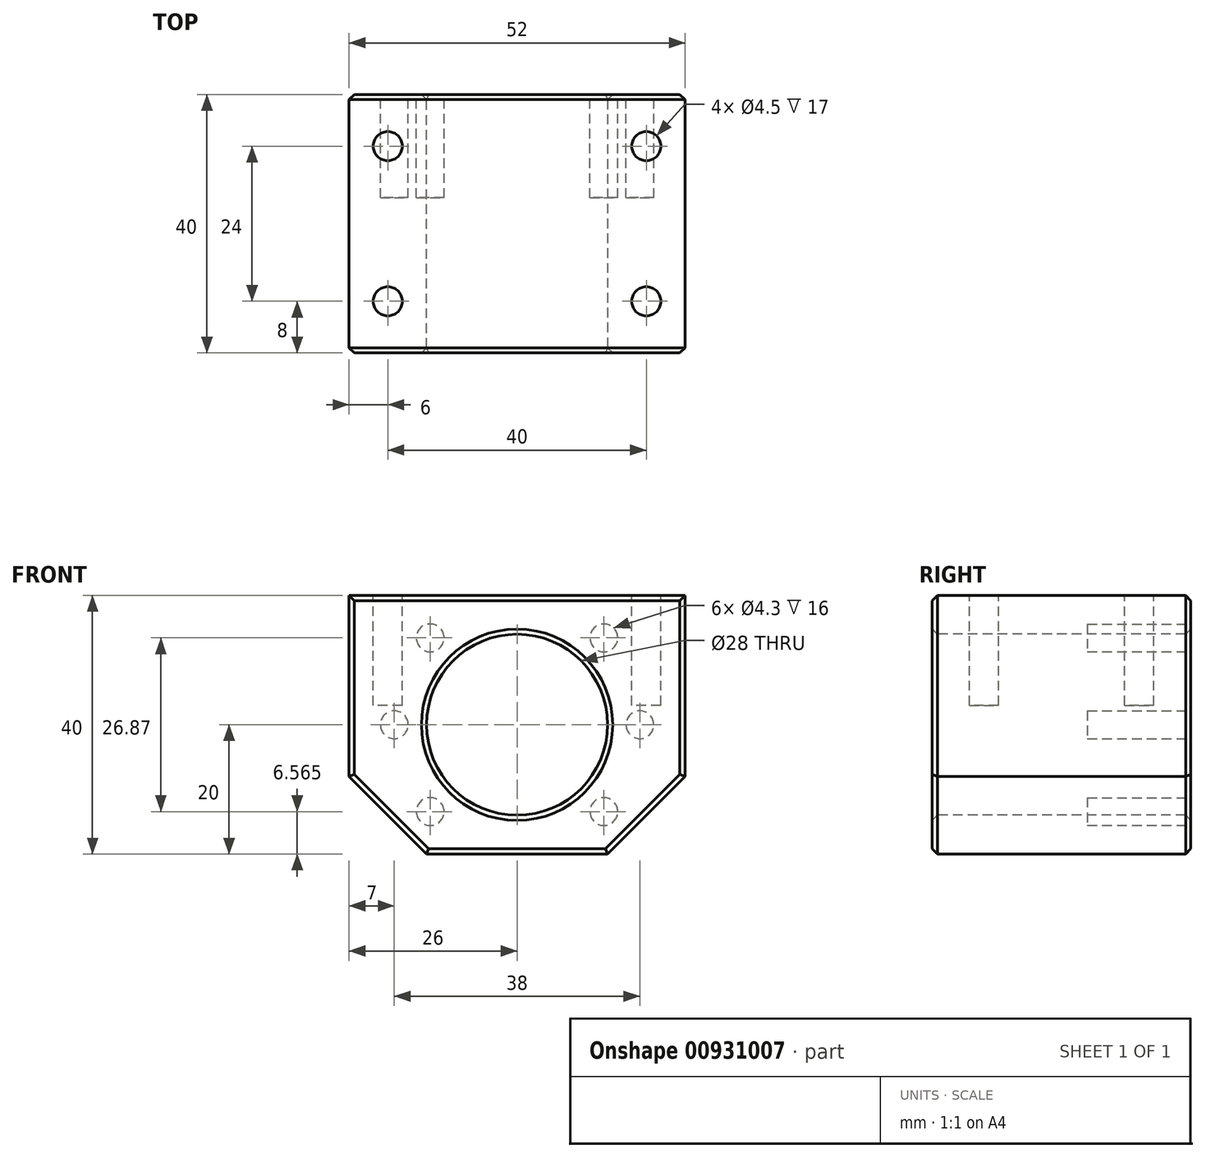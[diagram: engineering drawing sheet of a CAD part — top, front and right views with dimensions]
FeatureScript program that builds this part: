
annotation { "Feature Type Name" : "Feature", "Feature Type Description" : "" }
export const myFeature = defineFeature(function(context is Context, id is Id, definition is map)
    precondition{}
    {
        {
            var Q0;
            Q0=qCreatedBy(makeId("Top.planeOp"),FACE);
            var sketch = newSketch(context, id + "F0", { "sketchPlane" : qUnion([Q0])});
            skLineSegment(sketch, "E0.bottom", {"start": v(-26, -20) * mm, "end": v(26, -20) * mm});
            skLineSegment(sketch, "E0.top", {"start": v(-26, 20) * mm, "end": v(26, 20) * mm});
            skLineSegment(sketch, "E0.left", {"start": v(-26, -20) * mm, "end": v(-26, 20) * mm});
            skLineSegment(sketch, "E0.right", {"start": v(26, -20) * mm, "end": v(26, 20) * mm});
            skPoint(sketch, "E0.middle", {"position": v(0, 0) * mm});
            skSolve(sketch);
        }
        {
            var Q0;
            Q0=makeQuery(id+"F0.imprint","IMPRINT",FACE,{"disambiguationData":[TD([[makeQuery(id+"F0.imprint","IMPRINT",EDGE,{"derivedFrom":sQuery(id+"F0.wireOp",EDGE,"E0.bottom")}),1.0]])]});
            extrude(context, id + "F1", {"entities" : qUnion([Q0]), "depth" : 40 * mm, "offsetDistance" : 25 * mm});
        }
        {
            var Q0;
            Q0=makeQuery(id+"F1.opExtrude","SWEPT_FACE",FACE,{"disambiguationData":[OSD([sQuery(id+"F0.wireOp",EDGE,"E0.bottom")])]});
            var sketch = newSketch(context, id + "F2", { "sketchPlane" : qUnion([Q0])});
            skCircle(sketch, "E1", {"center": v(0, 20) * mm, "radius": 14 * mm});
            skSolve(sketch);
        }
        {
            var Q0;
            Q0=makeQuery(id+"F2.imprint","IMPRINT",FACE,{"disambiguationData":[TD([[makeQuery(id+"F2.imprint","IMPRINT",EDGE,{"derivedFrom":sQuery(id+"F2.wireOp",EDGE,"E1")}),1.0]])]});
            extrude(context, id + "F3", {"entities" : qUnion([Q0]), "operationType" : NewBodyOperationType.REMOVE, "endBound" : BoundingType.THROUGH_ALL, "oppositeDirection" : true, "depth" : 25 * mm, "offsetDistance" : 25 * mm});
        }
        {
            var Q0;
            Q0=makeQuery(id+"F1.opExtrude","CAP_FACE",FACE,{"disambiguationData":[OSD([sQuery(id+"F0.wireOp",EDGE,"E0.bottom"),sQuery(id+"F0.wireOp",EDGE,"E0.top"),sQuery(id+"F0.wireOp",EDGE,"E0.left"),sQuery(id+"F0.wireOp",EDGE,"E0.right")])],"isStart":false});
            var sketch = newSketch(context, id + "F4", { "sketchPlane" : qUnion([Q0])});
            skLineSegment(sketch, "E2.bottom", {"start": v(20, 12) * mm, "end": v(-20, 12) * mm, "construction": true});
            skLineSegment(sketch, "E2.top", {"start": v(20, -12) * mm, "end": v(-20, -12) * mm, "construction": true});
            skLineSegment(sketch, "E2.left", {"start": v(20, 12) * mm, "end": v(20, -12) * mm, "construction": true});
            skLineSegment(sketch, "E2.right", {"start": v(-20, 12) * mm, "end": v(-20, -12) * mm, "construction": true});
            skPoint(sketch, "E2.middle", {"position": v(0, 0) * mm});
            skCircle(sketch, "E3", {"center": v(-20, 12) * mm, "radius": 2.25 * mm});
            skCircle(sketch, "E4", {"center": v(-20, -12) * mm, "radius": 2.25 * mm});
            skCircle(sketch, "E5", {"center": v(20, -12) * mm, "radius": 2.25 * mm});
            skCircle(sketch, "E6", {"center": v(20, 12) * mm, "radius": 2.25 * mm});
            skSolve(sketch);
        }
        {
            var Q0;
            Q0 = qSketchRegion(id + "F4", true);
            extrude(context, id + "F5", {"entities" : qUnion([Q0]), "operationType" : NewBodyOperationType.REMOVE, "oppositeDirection" : true, "depth" : 17 * mm, "offsetDistance" : 25 * mm});
        }
        {
            var Q0;
            Q0=makeQuery(id+"F1.opExtrude","SWEPT_FACE",FACE,{"disambiguationData":[OSD([sQuery(id+"F0.wireOp",EDGE,"E0.top")])]});
            var sketch = newSketch(context, id + "F6", { "sketchPlane" : qUnion([Q0])});
            skCircle(sketch, "E7", {"center": v(0, 20) * mm, "radius": 19 * mm, "construction": true});
            skLineSegment(sketch, "E8", {"start": v(0, 20) * mm, "end": v(0, 40) * mm, "construction": true});
            skLineSegment(sketch, "E9", {"start": v(0, 20) * mm, "end": v(26, 20) * mm, "construction": true});
            skLineSegment(sketch, "E10", {"start": v(0, 20) * mm, "end": v(13.44, 33.44) * mm, "construction": true});
            skCircle(sketch, "E11", {"center": v(13.44, 33.44) * mm, "radius": 2.15 * mm});
            skCircle(sketch, "E12", {"center": v(19, 20) * mm, "radius": 2.15 * mm});
            skCircle(sketch, "E13.MirrorC", {"center": v(-13.44, 33.44) * mm, "radius": 2.15 * mm});
            skCircle(sketch, "E14.MirrorC", {"center": v(-19, 20) * mm, "radius": 2.15 * mm});
            skCircle(sketch, "E15.MirrorC", {"center": v(13.44, 6.56) * mm, "radius": 2.15 * mm});
            skCircle(sketch, "E16.MirrorC", {"center": v(-13.44, 6.56) * mm, "radius": 2.15 * mm});
            skSolve(sketch);
        }
        {
            var Q0;
            Q0 = qSketchRegion(id + "F6", true);
            extrude(context, id + "F7", {"entities" : qUnion([Q0]), "operationType" : NewBodyOperationType.REMOVE, "oppositeDirection" : true, "depth" : 16 * mm, "offsetDistance" : 25 * mm});
        }
        {
            var Q0;
            Q0=makeQuery(id+"F1.opExtrude","CAP_EDGE",EDGE,{"disambiguationData":[OSD([sQuery(id+"F0.wireOp",EDGE,"E0.left")])],"isStart":true});
            var Q1;
            Q1=makeQuery(id+"F1.opExtrude","CAP_EDGE",EDGE,{"disambiguationData":[OSD([sQuery(id+"F0.wireOp",EDGE,"E0.right")])],"isStart":true});
            chamfer(context, id + "F8", {"entities" : qUnion([Q0, Q1]), "width" : 12 * mm, "tangentPropagation" : true});
        }
        {
            var Q0;
            Q0=makeQuery(id+"F1.opExtrude","SWEPT_EDGE",EDGE,{"disambiguationData":[OSD([sQuery(id+"F0.wireOp",EDGE,"E0.top"),sQuery(id+"F0.wireOp",EDGE,"E0.left")])]});
            var Q1;
            Q1=makeQuery(id+"F8.opChamfer","BLEND_EDGE",EDGE,{"blendedFrom":[makeQuery(id+"F1.opExtrude","CAP_EDGE",EDGE,{"disambiguationData":[OSD([sQuery(id+"F0.wireOp",EDGE,"E0.left")])],"isStart":true}),makeQuery(id+"F1.opExtrude","SWEPT_FACE",FACE,{"disambiguationData":[OSD([sQuery(id+"F0.wireOp",EDGE,"E0.top")])]})],"blendedInto":[makeQuery(id+"F1.opExtrude","SWEPT_FACE",FACE,{"disambiguationData":[OSD([sQuery(id+"F0.wireOp",EDGE,"E0.top")])]})]});
            var Q2;
            Q2=makeQuery(id+"F1.opExtrude","CAP_EDGE",EDGE,{"disambiguationData":[OSD([sQuery(id+"F0.wireOp",EDGE,"E0.top")])],"isStart":true});
            var Q3;
            Q3=makeQuery(id+"F8.opChamfer","BLEND_EDGE",EDGE,{"blendedFrom":[makeQuery(id+"F1.opExtrude","CAP_EDGE",EDGE,{"disambiguationData":[OSD([sQuery(id+"F0.wireOp",EDGE,"E0.right")])],"isStart":true}),makeQuery(id+"F1.opExtrude","SWEPT_FACE",FACE,{"disambiguationData":[OSD([sQuery(id+"F0.wireOp",EDGE,"E0.top")])]})],"blendedInto":[makeQuery(id+"F1.opExtrude","SWEPT_FACE",FACE,{"disambiguationData":[OSD([sQuery(id+"F0.wireOp",EDGE,"E0.top")])]})]});
            var Q4;
            Q4=makeQuery(id+"F1.opExtrude","SWEPT_EDGE",EDGE,{"disambiguationData":[OSD([sQuery(id+"F0.wireOp",EDGE,"E0.top"),sQuery(id+"F0.wireOp",EDGE,"E0.right")])]});
            var Q5;
            Q5=makeQuery(id+"F1.opExtrude","CAP_EDGE",EDGE,{"disambiguationData":[OSD([sQuery(id+"F0.wireOp",EDGE,"E0.top")])],"isStart":false});
            var Q6;
            Q6=makeQuery(id+"F1.opExtrude","SWEPT_FACE",FACE,{"disambiguationData":[OSD([sQuery(id+"F0.wireOp",EDGE,"E0.bottom")])]});
            var Q7;
            Q7=makeQuery(id+"F3.boolean.opBoolean","INTERSECT",EDGE,{"derivedFrom":[makeQuery(id+"F1.opExtrude","SWEPT_FACE",FACE,{"disambiguationData":[OSD([sQuery(id+"F0.wireOp",EDGE,"E0.top")])]}),makeQuery(id+"F3.opExtrude","SWEPT_FACE",FACE,{"disambiguationData":[OSD([sQuery(id+"F2.wireOp",EDGE,"E1")])]})]});
            chamfer(context, id + "F9", {"entities" : qUnion([Q0, Q1, Q2, Q3, Q4, Q5, Q6, Q7]), "width" : 0.8 * mm, "tangentPropagation" : true});
        }
    });
